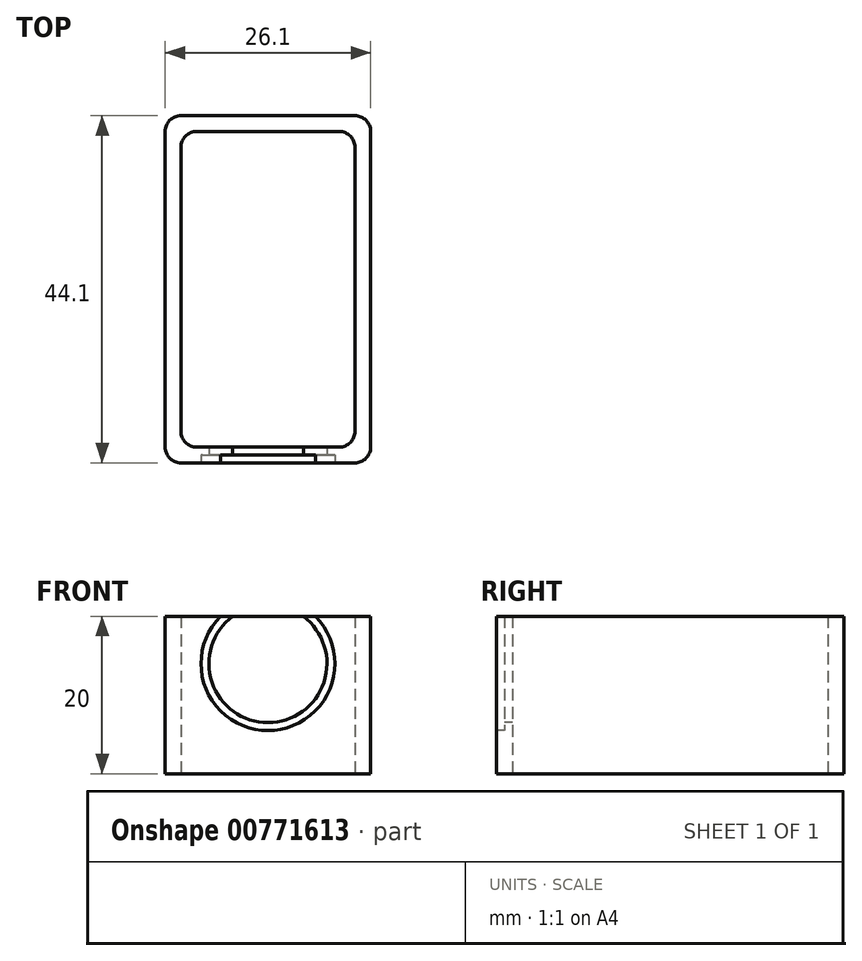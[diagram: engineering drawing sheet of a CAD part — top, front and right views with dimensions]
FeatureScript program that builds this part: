
annotation { "Feature Type Name" : "Feature", "Feature Type Description" : "" }
export const myFeature = defineFeature(function(context is Context, id is Id, definition is map)
    precondition{}
    {
        {
            var Q0;
            Q0=qCreatedBy(makeId("Top.planeOp"),FACE);
            var sketch = newSketch(context, id + "F0", { "sketchPlane" : qUnion([Q0])});
            skLineSegment(sketch, "E0.bottom", {"start": v(-11.05, 20.05) * mm, "end": v(11.05, 20.05) * mm});
            skLineSegment(sketch, "E0.top", {"start": v(-11.05, -20.05) * mm, "end": v(11.05, -20.05) * mm});
            skLineSegment(sketch, "E0.left", {"start": v(-11.05, 20.05) * mm, "end": v(-11.05, -20.05) * mm});
            skLineSegment(sketch, "E0.right", {"start": v(11.05, 20.05) * mm, "end": v(11.05, -20.05) * mm});
            skLineSegment(sketch, "E1.0", {"start": v(-13.05, 22.05) * mm, "end": v(13.05, 22.05) * mm});
            skLineSegment(sketch, "E1.1", {"start": v(-13.05, 22.05) * mm, "end": v(-13.05, -22.05) * mm});
            skLineSegment(sketch, "E1.2", {"start": v(-13.05, -22.05) * mm, "end": v(13.05, -22.05) * mm});
            skLineSegment(sketch, "E1.3", {"start": v(13.05, 22.05) * mm, "end": v(13.05, -22.05) * mm});
            skLineSegment(sketch, "E2", {"start": v(-11.05, -20.05) * mm, "end": v(11.05, 20.05) * mm, "construction": true});
            skSolve(sketch);
        }
        {
            var Q0;
            Q0 = qSketchRegion(id + "F0", true);
            extrude(context, id + "F1", {"entities" : qUnion([Q0]), "endBound" : BoundingType.SYMMETRIC, "depth" : 20 * mm, "offsetDistance" : 25 * mm});
        }
        {
            var Q0;
            Q0=makeQuery(id+"F1.opExtrude","SWEPT_FACE",FACE,{"disambiguationData":[OSD([sQuery(id+"F0.wireOp",EDGE,"E1.2")])]});
            var sketch = newSketch(context, id + "F2", { "sketchPlane" : qUnion([Q0])});
            skCircle(sketch, "E3", {"center": v(0, 4) * mm, "radius": 7.5 * mm});
            skLineSegment(sketch, "E4", {"start": v(0, 0) * mm, "end": v(0, 10) * mm, "construction": true});
            skSolve(sketch);
        }
        {
            var Q0;
            Q0 = qSketchRegion(id + "F2", true);
            extrude(context, id + "F3", {"entities" : qUnion([Q0]), "operationType" : NewBodyOperationType.REMOVE, "oppositeDirection" : true, "depth" : 10 * mm, "offsetDistance" : 25 * mm});
        }
        {
            var Q0;
            Q0=makeQuery(id+"F1.opExtrude","SWEPT_FACE",FACE,{"disambiguationData":[OSD([sQuery(id+"F0.wireOp",EDGE,"E1.2")])]});
            var sketch = newSketch(context, id + "F4", { "sketchPlane" : qUnion([Q0])});
            skCircle(sketch, "E5", {"center": v(0, 4) * mm, "radius": 7.5 * mm});
            skLineSegment(sketch, "E6", {"start": v(0, 0) * mm, "end": v(0, 9.93) * mm, "construction": true});
            skCircle(sketch, "E7.0", {"center": v(0, 4) * mm, "radius": 8.5 * mm});
            skSolve(sketch);
        }
        {
            var Q0;
            Q0 = qSketchRegion(id + "F4", true);
            extrude(context, id + "F5", {"entities" : qUnion([Q0]), "operationType" : NewBodyOperationType.REMOVE, "oppositeDirection" : true, "depth" : 1 * mm, "offsetDistance" : 25 * mm});
        }
        {
            var Q0;
            Q0=makeQuery(id+"F1.opExtrude","SWEPT_EDGE",EDGE,{"disambiguationData":[OSD([sQuery(id+"F0.wireOp",EDGE,"E1.1"),sQuery(id+"F0.wireOp",EDGE,"E1.2")])]});
            var Q1;
            Q1=makeQuery(id+"F1.opExtrude","SWEPT_EDGE",EDGE,{"disambiguationData":[OSD([sQuery(id+"F0.wireOp",EDGE,"E1.2"),sQuery(id+"F0.wireOp",EDGE,"E1.3")])]});
            var Q2;
            Q2=makeQuery(id+"F1.opExtrude","SWEPT_EDGE",EDGE,{"disambiguationData":[OSD([sQuery(id+"F0.wireOp",EDGE,"E1.0"),sQuery(id+"F0.wireOp",EDGE,"E1.3")])]});
            var Q3;
            Q3=makeQuery(id+"F1.opExtrude","SWEPT_EDGE",EDGE,{"disambiguationData":[OSD([sQuery(id+"F0.wireOp",EDGE,"E1.0"),sQuery(id+"F0.wireOp",EDGE,"E1.1")])]});
            fillet(context, id + "F6", {"entities" : qUnion([Q0, Q1, Q2, Q3]), "radius" : 2 * mm, "tangentPropagation" : true, "allowEdgeOverflow" : false});
        }
        {
            var Q0;
            Q0=makeQuery(id+"F1.opExtrude","SWEPT_EDGE",EDGE,{"disambiguationData":[OSD([sQuery(id+"F0.wireOp",EDGE,"E0.bottom"),sQuery(id+"F0.wireOp",EDGE,"E0.left")])]});
            var Q1;
            Q1=makeQuery(id+"F1.opExtrude","SWEPT_EDGE",EDGE,{"disambiguationData":[OSD([sQuery(id+"F0.wireOp",EDGE,"E0.bottom"),sQuery(id+"F0.wireOp",EDGE,"E0.right")])]});
            var Q2;
            Q2=makeQuery(id+"F1.opExtrude","SWEPT_EDGE",EDGE,{"disambiguationData":[OSD([sQuery(id+"F0.wireOp",EDGE,"E0.top"),sQuery(id+"F0.wireOp",EDGE,"E0.right")])]});
            var Q3;
            Q3=makeQuery(id+"F1.opExtrude","SWEPT_EDGE",EDGE,{"disambiguationData":[OSD([sQuery(id+"F0.wireOp",EDGE,"E0.top"),sQuery(id+"F0.wireOp",EDGE,"E0.left")])]});
            fillet(context, id + "F7", {"entities" : qUnion([Q0, Q1, Q2, Q3]), "radius" : 2 * mm, "tangentPropagation" : true, "allowEdgeOverflow" : false});
        }
    });
